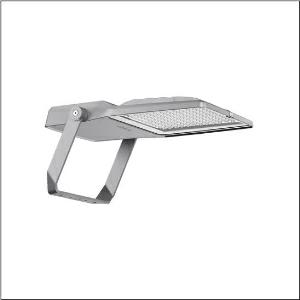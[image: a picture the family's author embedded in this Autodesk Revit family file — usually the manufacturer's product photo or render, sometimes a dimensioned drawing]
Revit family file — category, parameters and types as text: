
# Revit family: floodlight_fl_21_iq_midi___rs12_5xa7782e3b1a_df6b
name_source: partatom
category: Lighting Fixtures
units: mm (PartAtom-declared; Revit-internal decimal feet)

## family parameters
Cut with Voids When Loaded = No
Host = Face
Light Source = No
Part Type = Normal
Room Calculation Point = No
Round Connector Dimension = Use Diameter
Shared = No

## types (1)
- --- (1 x LED, 23000 lm, 208.1 W, 3000K)
    Apparent Load = 208 VA
    CIE Flux Codes = 79 92 99 100 100
    Color Rendering = 80
    Color Temperature = 3000K
    Default Elevation = 1800 mm
    Description = Floodlight FL 21 iQ midi, floodlight, primary light control with lens, of PMMA, primary optical cover: protective disc, of toughened safety glass, transparent, light distribution: RS12, light emission: direct distribution, installation type: surface-mounted, LED, High Power LED, rated luminous flux: 23.000lm, luminous efficacy: 111lm/W, light colour: 830, colour temperature: 3000K, control gear: ECG iQ, control: optimised constant luminous flux control (CLO 2.0), Desk-Remote (wireless, voltage-free reading and setting of iQ features in the workshop via application-optimized NFC function/RFID function), Smart-Wire, Night-Set, Temp-Guard, Street-Remote, Auto-Match, with terminal, 6-pole, mains connection: 220..240V, AC, 50/60Hz, start of lifetime: 208W, end of service life: 227W, reduction: 90W, luminaire housing, of diecast aluminium, powder-coated, Siteco® metallic grey (DB 702S), corrosivity category C5 mid according to DIN EN ISO 12944, sealing non-destructively replaceable, mounting bracket, of steel, galvanised, powder-coated, Siteco® metallic grey (DB 702S), protection rating (complete): IP66, insulation class (complete): insulation class II (safety insulation), certification: CE, protection symbol: D, impact resistance: IK08, permissible operating ambient temperature: -40..+40°C, permissible operating ambient temperature for outdoor applications: -40..+50°C, standard: DIN EN 12944, LABS conformity tested according to VDMA 24364:2018-05, packaging unit: 1 piece

Light Distribution: RS12
    Height = 76 mm
    Lamp = 1 x LED
    Lamp Light Flux = 23000 lm
    Lamp Power = 208.1 W
    Lamp count = 1
    Length = 657 mm
    Luminous efficacy = 111 lm/W
    Manufacturer = Siteco
    ModVariant = No
    Model = 5XA7782E3B1A
    Number of Poles = 1
    OnlyDefault = Yes
    Power Factor = 1
    Product Name = Floodlight FL 21 iQ midi | RS12
    Product group = floodlight | pylon annexe
    ProductGroupID = 6200
    Protection Class = Protection class II
    Protection Degree = IP 66
    RLX_Detail_Level = 1
    RLX_Emergency_Light_Flux = 0 lm
    RLX_Emergency_Type = 0
    RLX_Emergency_Type_DB = No
    RlxData = <blob elided: 141289 chars, md5=7f098842>
    Socket = socket
    Standby Power = 0 W
    System Light Flux = 23000 lm
    System Power = 208 W
    Type Comments = factory setting: luminous flux: 100 % | dim-lin: 254 | 710 mA
    Type Image = l_1006876.jpg
    URL = http://relux.com
    VarID = @adj_037907
    Voltage = 0 V
    Weight = 0.00 kg
    Width = 442 mm

## geometry (parser evidence)
native form markers: Blend x4, Sweep x13
no freeform markers — native parametric forms only
